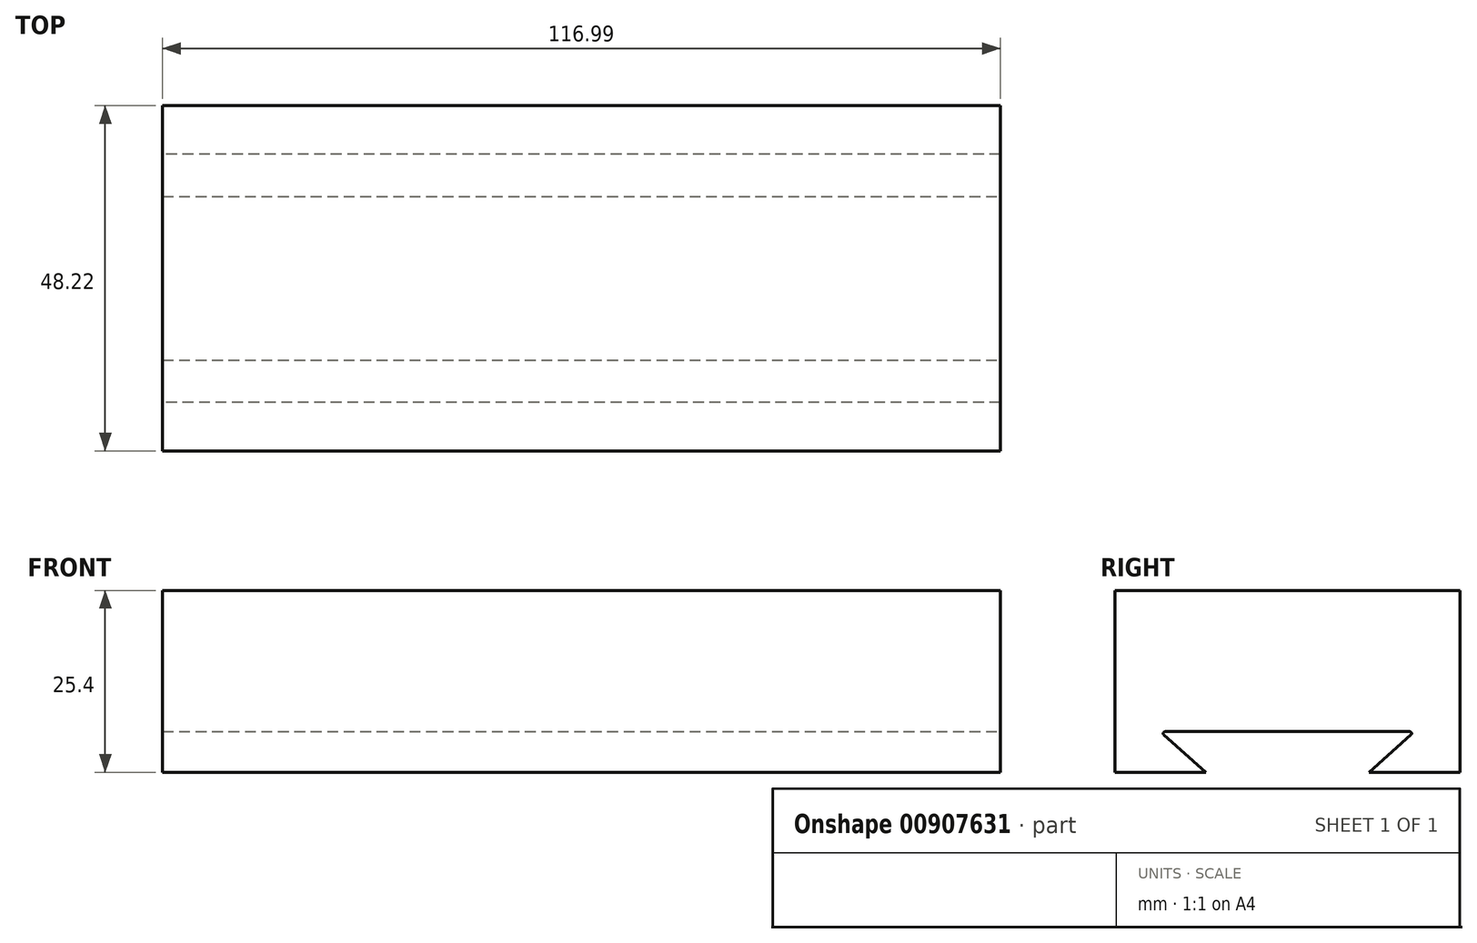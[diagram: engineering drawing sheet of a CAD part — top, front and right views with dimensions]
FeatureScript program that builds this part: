
annotation { "Feature Type Name" : "Feature", "Feature Type Description" : "" }
export const myFeature = defineFeature(function(context is Context, id is Id, definition is map)
    precondition{}
    {
        {
            var Q0;
            Q0=qCreatedBy(makeId("Top.planeOp"),FACE);
            var sketch = newSketch(context, id + "F0", { "sketchPlane" : qUnion([Q0])});
            skLineSegment(sketch, "E0.bottom", {"start": v(-56.05, -22.33) * mm, "end": v(60.94, -22.33) * mm});
            skLineSegment(sketch, "E0.top", {"start": v(-56.05, 25.89) * mm, "end": v(60.94, 25.89) * mm});
            skLineSegment(sketch, "E0.left", {"start": v(-56.05, -22.33) * mm, "end": v(-56.05, 25.89) * mm});
            skLineSegment(sketch, "E0.right", {"start": v(60.94, -22.33) * mm, "end": v(60.94, 25.89) * mm});
            skSolve(sketch);
        }
        {
            var Q0;
            Q0 = qSketchRegion(id + "F0", true);
            extrude(context, id + "F1", {"entities" : qUnion([Q0]), "depth" : 25.4 * mm, "offsetDistance" : 25.4 * mm});
        }
        {
            var Q0;
            Q0=makeQuery(id+"F1.opExtrude","SWEPT_FACE",FACE,{"disambiguationData":[OSD([sQuery(id+"F0.wireOp",EDGE,"E0.right")])]});
            var sketch = newSketch(context, id + "F2", { "sketchPlane" : qUnion([Q0])});
            skLineSegment(sketch, "E1", {"start": v(-9.63, 0) * mm, "end": v(-15.98, 5.67) * mm});
            skLineSegment(sketch, "E2", {"start": v(-15.98, 5.67) * mm, "end": v(19.54, 5.67) * mm});
            skLineSegment(sketch, "E3", {"start": v(19.54, 5.67) * mm, "end": v(13.19, 0) * mm});
            skLineSegment(sketch, "E4", {"start": v(13.19, 0) * mm, "end": v(-9.63, 0) * mm});
            skSolve(sketch);
        }
        {
            var Q0;
            Q0 = qSketchRegion(id + "F2", true);
            extrude(context, id + "F3", {"entities" : qUnion([Q0]), "operationType" : NewBodyOperationType.REMOVE, "endBound" : BoundingType.THROUGH_ALL, "oppositeDirection" : true, "depth" : 25.4 * mm, "offsetDistance" : 25.4 * mm});
        }
        {
            var Q0;
            Q0=makeQuery(id+"F3.boolean.opBoolean","COPY",EDGE,{"derivedFrom":makeQuery(id+"F3.opExtrude","SWEPT_EDGE",EDGE,{"disambiguationData":[OSD([sQuery(id+"F2.wireOp",EDGE,"E1"),sQuery(id+"F2.wireOp",EDGE,"E2")])]})});
            var Q1;
            Q1=makeQuery(id+"F3.boolean.opBoolean","COPY",EDGE,{"derivedFrom":makeQuery(id+"F3.opExtrude","SWEPT_EDGE",EDGE,{"disambiguationData":[OSD([sQuery(id+"F2.wireOp",EDGE,"E2"),sQuery(id+"F2.wireOp",EDGE,"E3")])]})});
            fillet(context, id + "F4", {"entities" : qUnion([Q0, Q1]), "radius" : 0.25 * mm, "tangentPropagation" : true, "allowEdgeOverflow" : false});
        }
    });
